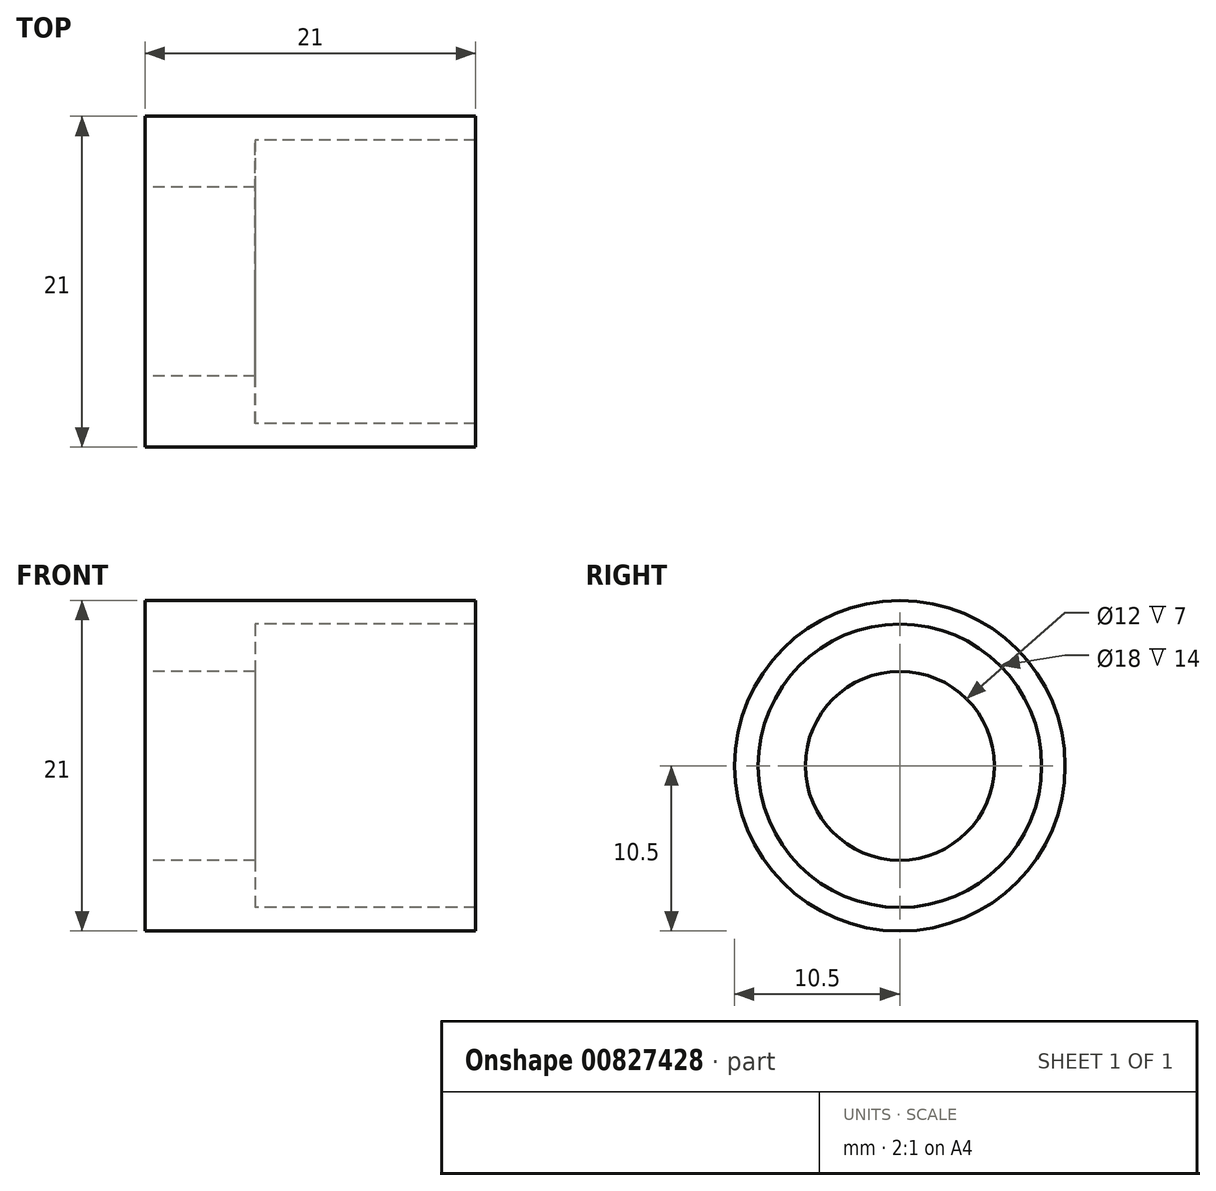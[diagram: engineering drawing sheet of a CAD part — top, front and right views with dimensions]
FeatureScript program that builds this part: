
annotation { "Feature Type Name" : "Feature", "Feature Type Description" : "" }
export const myFeature = defineFeature(function(context is Context, id is Id, definition is map)
    precondition{}
    {
        {
            var Q0;
            Q0=qCreatedBy(makeId("Front.planeOp"),FACE);
            var sketch = newSketch(context, id + "F0", { "sketchPlane" : qUnion([Q0])});
            skLineSegment(sketch, "E0", {"start": v(-81.06, 0) * mm, "end": v(107.29, 0) * mm, "construction": true});
            skLineSegment(sketch, "E1", {"start": v(0, 6) * mm, "end": v(7, 6) * mm});
            skLineSegment(sketch, "E2", {"start": v(7, 6) * mm, "end": v(7, 9) * mm});
            skLineSegment(sketch, "E3", {"start": v(7, 9) * mm, "end": v(21, 9) * mm});
            skLineSegment(sketch, "E4", {"start": v(21, 9) * mm, "end": v(21, 10.5) * mm});
            skLineSegment(sketch, "E5", {"start": v(21, 10.5) * mm, "end": v(0, 10.5) * mm});
            skLineSegment(sketch, "E6", {"start": v(0, 10.5) * mm, "end": v(0, 6) * mm});
            skSolve(sketch);
        }
        {
            var Q0;
            Q0=makeQuery(id+"F0.imprint","IMPRINT",FACE,{"disambiguationData":[TD([[makeQuery(id+"F0.imprint","IMPRINT",EDGE,{"derivedFrom":sQuery(id+"F0.wireOp",EDGE,"E1")}),1.0]])]});
            var Q1;
            Q1=sQuery(id+"F0.wireOp",EDGE,"E0");
            revolve(context, id + "F1", {"surfaceOperationType" : NewSurfaceOperationType.NEW, "entities" : qUnion([Q0]), "axis" : qUnion([Q1]), "revolveType" : RevolveType.FULL});
        }
    });
